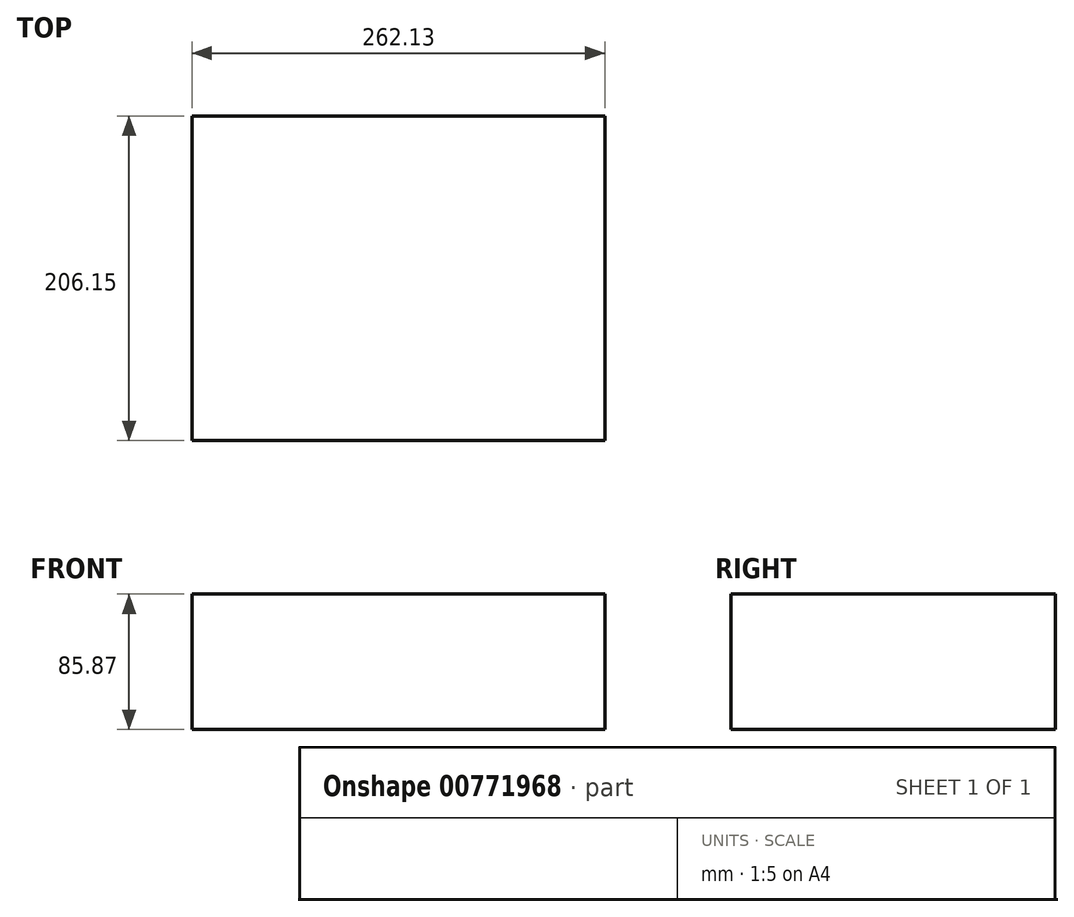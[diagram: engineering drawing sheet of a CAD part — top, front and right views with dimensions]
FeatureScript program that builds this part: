
annotation { "Feature Type Name" : "Feature", "Feature Type Description" : "" }
export const myFeature = defineFeature(function(context is Context, id is Id, definition is map)
    precondition{}
    {
        {
            var Q0;
            Q0=qCreatedBy(makeId("Right.planeOp"),FACE);
            var sketch = newSketch(context, id + "F0", { "sketchPlane" : qUnion([Q0])});
            skLineSegment(sketch, "E0.bottom", {"start": v(0, 0) * mm, "end": v(206.15, 0) * mm});
            skLineSegment(sketch, "E0.top", {"start": v(0, -85.87) * mm, "end": v(206.15, -85.87) * mm});
            skLineSegment(sketch, "E0.left", {"start": v(0, 0) * mm, "end": v(0, -85.87) * mm});
            skLineSegment(sketch, "E0.right", {"start": v(206.15, 0) * mm, "end": v(206.15, -85.87) * mm});
            skSolve(sketch);
        }
        {
            var Q0;
            Q0 = qSketchRegion(id + "F0", true);
            extrude(context, id + "F1", {"entities" : qUnion([Q0]), "depth" : 262.13 * mm, "offsetDistance" : 25.4 * mm});
        }
        {
            var Q0;
            Q0=makeQuery(id+"F1.opExtrude","SWEPT_FACE",FACE,{"disambiguationData":[OSD([sQuery(id+"F0.wireOp",EDGE,"E0.bottom")])]});
            var sketch = newSketch(context, id + "F2", { "sketchPlane" : qUnion([Q0])});
            skLineSegment(sketch, "E1.bottom", {"start": v(20.66, 188.83) * mm, "end": v(242.57, 188.83) * mm});
            skLineSegment(sketch, "E1.top", {"start": v(20.66, 18.33) * mm, "end": v(242.57, 18.33) * mm});
            skLineSegment(sketch, "E1.left", {"start": v(20.66, 188.83) * mm, "end": v(20.66, 18.33) * mm});
            skLineSegment(sketch, "E1.right", {"start": v(242.57, 188.83) * mm, "end": v(242.57, 18.33) * mm});
            skSolve(sketch);
        }
        {
            var Q0;
            Q0 = qSketchRegion(id + "F2", true);
            extrude(context, id + "F3", {"entities" : qUnion([Q0]), "operationType" : NewBodyOperationType.ADD, "oppositeDirection" : true, "depth" : 15.24 * mm, "offsetDistance" : 25.4 * mm});
        }
        {
            var Q0;
            Q0=makeQuery(id+"F1.opExtrude","SWEPT_FACE",FACE,{"disambiguationData":[OSD([sQuery(id+"F0.wireOp",EDGE,"E0.bottom")])]});
            var sketch = newSketch(context, id + "F4", { "sketchPlane" : qUnion([Q0])});
            skLineSegment(sketch, "E2.bottom", {"start": v(15.85, 193.64) * mm, "end": v(245.24, 193.64) * mm});
            skLineSegment(sketch, "E2.top", {"start": v(15.85, 15.66) * mm, "end": v(245.24, 15.66) * mm});
            skLineSegment(sketch, "E2.left", {"start": v(15.85, 193.64) * mm, "end": v(15.85, 15.66) * mm});
            skLineSegment(sketch, "E2.right", {"start": v(245.24, 193.64) * mm, "end": v(245.24, 15.66) * mm});
            skSolve(sketch);
        }
        {
            var Q0;
            Q0 = qSketchRegion(id + "F4", true);
            extrude(context, id + "F5", {"entities" : qUnion([Q0]), "operationType" : NewBodyOperationType.ADD, "oppositeDirection" : true, "depth" : 40.4 * mm, "offsetDistance" : 25.4 * mm});
        }
    });
